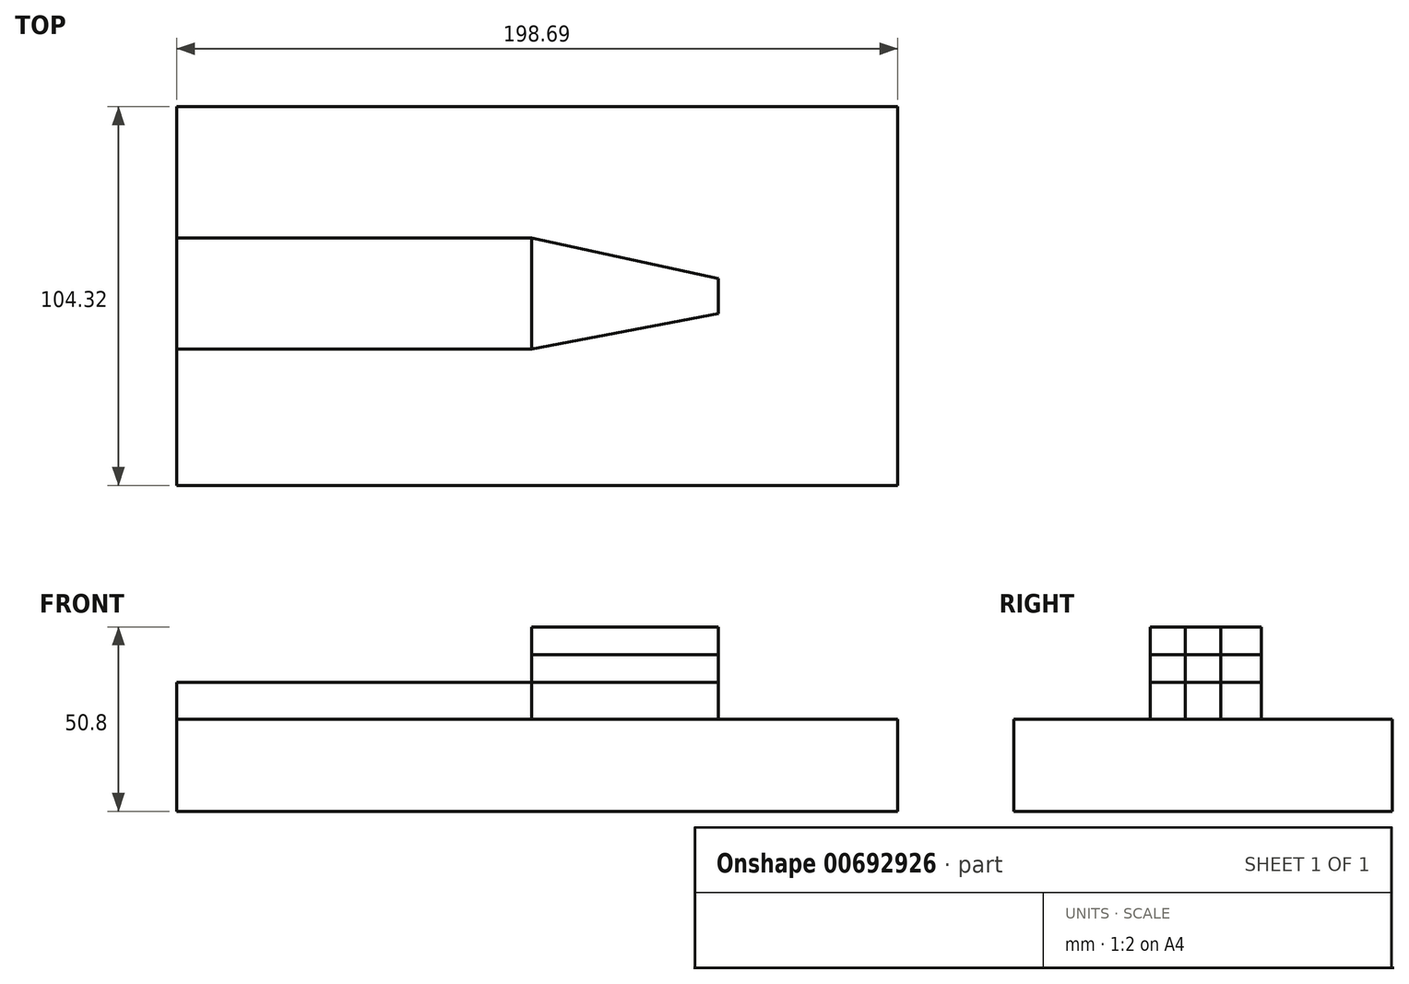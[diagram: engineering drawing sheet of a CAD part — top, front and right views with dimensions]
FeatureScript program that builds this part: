
annotation { "Feature Type Name" : "Feature", "Feature Type Description" : "" }
export const myFeature = defineFeature(function(context is Context, id is Id, definition is map)
    precondition{}
    {
        {
            var Q0;
            Q0=qCreatedBy(makeId("Top.planeOp"),FACE);
            var sketch = newSketch(context, id + "F0", { "sketchPlane" : qUnion([Q0])});
            skLineSegment(sketch, "E0.left", {"start": v(-149.3, 52.16) * mm, "end": v(-149.3, -52.16) * mm});
            skPoint(sketch, "E0.middle", {"position": v(0, 0) * mm});
            skLineSegment(sketch, "E1", {"start": v(-149.3, 52.16) * mm, "end": v(49.39, 52.16) * mm});
            skLineSegment(sketch, "E2", {"start": v(49.39, 52.16) * mm, "end": v(49.39, -52.16) * mm});
            skLineSegment(sketch, "E3", {"start": v(49.39, -52.16) * mm, "end": v(-149.3, -52.16) * mm});
            skSolve(sketch);
        }
        {
            var Q0;
            Q0 = qSketchRegion(id + "F0", true);
            var Q1;
            Q1=makeQuery(id+"F0.imprint","IMPRINT",FACE,{"disambiguationData":[TD([[makeQuery(id+"F0.imprint","IMPRINT",EDGE,{"derivedFrom":sQuery(id+"F0.wireOp",EDGE,"E0.bottom")}),-1.0]])]});
            extrude(context, id + "F1", {"entities" : qUnion([Q0, Q1]), "oppositeDirection" : true, "depth" : 25.4 * mm, "offsetDistance" : 25.4 * mm});
        }
        {
            var Q0;
            Q0=makeQuery(id+"F1.opExtrude","CAP_FACE",FACE,{"disambiguationData":[OSD([sQuery(id+"F0.wireOp",EDGE,"E0.bottom"),sQuery(id+"F0.wireOp",EDGE,"E0.top"),sQuery(id+"F0.wireOp",EDGE,"E0.left"),sQuery(id+"F0.wireOp",EDGE,"E0.right")])],"isStart":true});
            var sketch = newSketch(context, id + "F2", { "sketchPlane" : qUnion([Q0])});
            skLineSegment(sketch, "E4", {"start": v(-51.41, 16.02) * mm, "end": v(0, 4.87) * mm});
            skLineSegment(sketch, "E5", {"start": v(0, 4.87) * mm, "end": v(0, -4.87) * mm});
            skLineSegment(sketch, "E6", {"start": v(0, -4.87) * mm, "end": v(-51.41, -14.6) * mm});
            skLineSegment(sketch, "E7", {"start": v(-51.41, 16.02) * mm, "end": v(-149.21, 16.02) * mm});
            skLineSegment(sketch, "E8", {"start": v(-149.21, 16.02) * mm, "end": v(-149.21, -14.6) * mm});
            skLineSegment(sketch, "E9", {"start": v(-149.21, -14.6) * mm, "end": v(-51.41, -14.6) * mm});
            skSolve(sketch);
        }
        {
            var Q0;
            Q0 = qSketchRegion(id + "F2", true);
            extrude(context, id + "F3", {"entities" : qUnion([Q0]), "depth" : 10.16 * mm, "offsetDistance" : 25.4 * mm});
        }
        {
            var Q0;
            Q0=makeQuery(id+"F3.opExtrude","CAP_FACE",FACE,{"disambiguationData":[OSD([sQuery(id+"F2.wireOp",EDGE,"E4"),sQuery(id+"F2.wireOp",EDGE,"E5"),sQuery(id+"F2.wireOp",EDGE,"E6"),sQuery(id+"F2.wireOp",EDGE,"E7"),sQuery(id+"F2.wireOp",EDGE,"E8"),sQuery(id+"F2.wireOp",EDGE,"E9")])],"isStart":false});
            var sketch = newSketch(context, id + "F4", { "sketchPlane" : qUnion([Q0])});
            skLineSegment(sketch, "E10", {"start": v(-51.41, 16.02) * mm, "end": v(0, 4.87) * mm});
            skLineSegment(sketch, "E11", {"start": v(0, 4.87) * mm, "end": v(0, -4.87) * mm});
            skLineSegment(sketch, "E12", {"start": v(0, -4.87) * mm, "end": v(-51.41, -14.6) * mm});
            skLineSegment(sketch, "E13", {"start": v(-51.41, -14.6) * mm, "end": v(-51.41, 16.02) * mm});
            skSolve(sketch);
        }
        {
            var Q0;
            Q0 = qSketchRegion(id + "F4", true);
            extrude(context, id + "F5", {"entities" : qUnion([Q0]), "depth" : 7.62 * mm, "offsetDistance" : 25.4 * mm});
        }
        {
            var Q0;
            Q0=makeQuery(id+"F5.opExtrude","CAP_FACE",FACE,{"disambiguationData":[OSD([sQuery(id+"F4.wireOp",EDGE,"E10"),sQuery(id+"F4.wireOp",EDGE,"E11"),sQuery(id+"F4.wireOp",EDGE,"E12"),sQuery(id+"F4.wireOp",EDGE,"E13")])],"isStart":false});
            var sketch = newSketch(context, id + "F6", { "sketchPlane" : qUnion([Q0])});
            skLineSegment(sketch, "E14", {"start": v(-51.41, 16.02) * mm, "end": v(0, 4.87) * mm});
            skLineSegment(sketch, "E15", {"start": v(0, 4.87) * mm, "end": v(0, -4.87) * mm});
            skLineSegment(sketch, "E16", {"start": v(0, -4.87) * mm, "end": v(-51.41, -14.6) * mm});
            skLineSegment(sketch, "E17", {"start": v(-51.41, -14.6) * mm, "end": v(-51.41, 16.02) * mm});
            skSolve(sketch);
        }
        {
            var Q0;
            Q0 = qSketchRegion(id + "F6", true);
            extrude(context, id + "F7", {"entities" : qUnion([Q0]), "depth" : 7.62 * mm, "offsetDistance" : 25.4 * mm});
        }
    });
